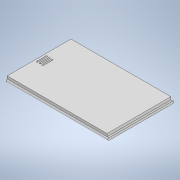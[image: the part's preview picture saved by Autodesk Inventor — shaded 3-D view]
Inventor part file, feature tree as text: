
AUTODESK INVENTOR PART (.ipt)
format: ipt  version: 2020.2 (Build 242310000, 310)  size: 158,208 bytes
history: native  units: mm
features: extrude x4, sketch x4
ambient origin geometry x8: Origin, YZ Plane, XZ Plane, XY Plane, X Axis, Y Axis, Z Axis, Center Point
bodies: Solid1 (feature_tree)
feature tree (8):
  extrude  "Extrusion1"  TaperAngle=90.0deg  [1 undecoded]
  extrude  "Extrusion2"  Depth=110.0mm TaperAngle=0.0deg
  extrude  "Extrusion3"  TaperAngle=0.0deg  [1 undecoded]
  extrude  "Extrusion4"  Depth=34.5mm
  sketch  "Sketch1"  dims[d0=34.5mm d1=90.0deg]
  sketch  "Sketch2"  dims[d2=2.5mm d3=110.0mm d4=0.0mm]
  sketch  "Sketch3"  dims[d5=108.0mm d6=0.0mm]
  sketch  "Sketch4"  dims[d7=34.5mm d8=34.5mm d9=90.0deg d10=3.0mm d11=0.0mm d12=3.0mm d13=3.0mm d14=3.0mm d15=180.0deg d16=5.0mm d17=90.0deg d18=1.5mm d19=5.0mm d20=1.5mm d21=5.0mm d22=1.5mm d23=2.0mm d24=-7.853982mm d25=1.5mm d26=20.0mm d27=90.0deg d28=2.5mm d29=2.0mm d30=-7.853982mm]
note: 2 required parameter values undecoded (feature->parameter linkage not recoverable at this tier; creation-order binding heuristic only, values carry confidence <= 0.55)
